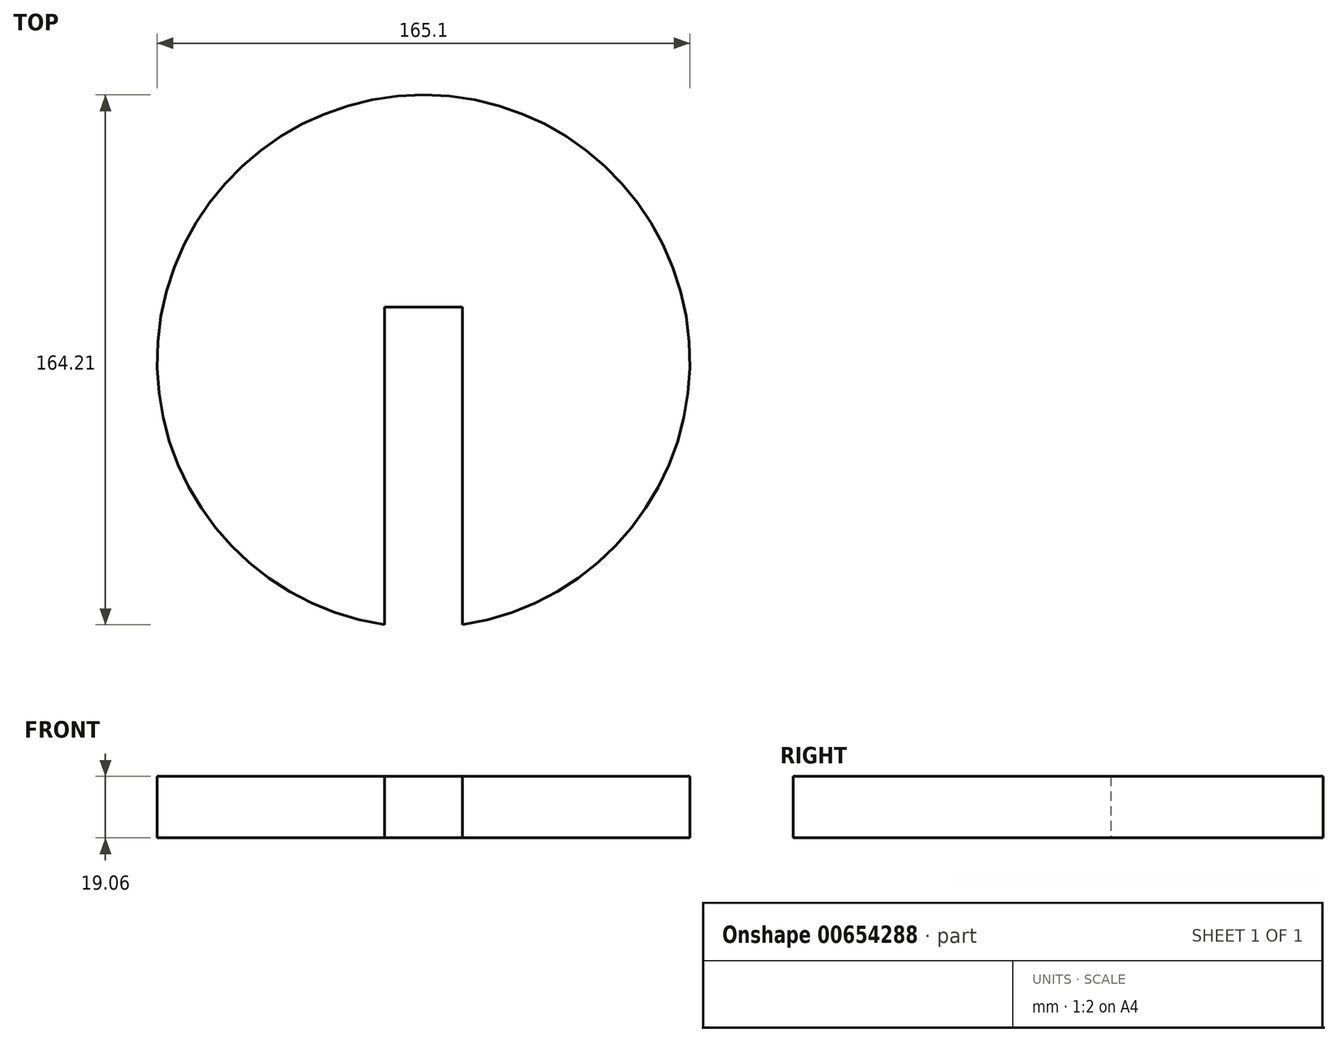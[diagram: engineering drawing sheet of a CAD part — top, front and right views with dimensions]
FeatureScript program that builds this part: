
annotation { "Feature Type Name" : "Feature", "Feature Type Description" : "" }
export const myFeature = defineFeature(function(context is Context, id is Id, definition is map)
    precondition{}
    {
        {
            var Q0;
            Q0=qCreatedBy(makeId("Top.planeOp"),FACE);
            var sketch = newSketch(context, id + "F0", { "sketchPlane" : qUnion([Q0])});
            skCircle(sketch, "E0", {"center": v(0, 0) * mm, "radius": 82.55 * mm});
            skSolve(sketch);
        }
        {
            var Q0;
            Q0=qSketchRegion(id+"F0",true);
            extrude(context, id + "F1", {"entities" : qUnion([Q0]), "endBound" : BoundingType.SYMMETRIC, "depth" : 19.05 * mm, "offsetDistance" : 25.4 * mm});
        }
        {
            var Q0;
            Q0=qCreatedBy(makeId("Top.planeOp"),FACE);
            var sketch = newSketch(context, id + "F2", { "sketchPlane" : qUnion([Q0])});
            skLineSegment(sketch, "E1.top", {"start": v(12.07, -82.62) * mm, "end": v(-12.06, -82.62) * mm});
            skPoint(sketch, "E1.middle", {"position": v(0, 0) * mm});
            skLineSegment(sketch, "E2", {"start": v(-12.06, 16.82) * mm, "end": v(12.07, 16.82) * mm});
            skLineSegment(sketch, "E3", {"start": v(-12.06, 16.82) * mm, "end": v(-12.06, -82.62) * mm});
            skLineSegment(sketch, "E4", {"start": v(12.07, 16.82) * mm, "end": v(12.07, -82.62) * mm});
            skSolve(sketch);
        }
        {
            var Q0;
            Q0=qSketchRegion(id+"F2",true);
            extrude(context, id + "F3", {"entities" : qUnion([Q0]), "operationType" : NewBodyOperationType.REMOVE, "endBound" : BoundingType.SYMMETRIC, "depth" : 19.05 * mm, "offsetDistance" : 25.4 * mm});
        }
    });
